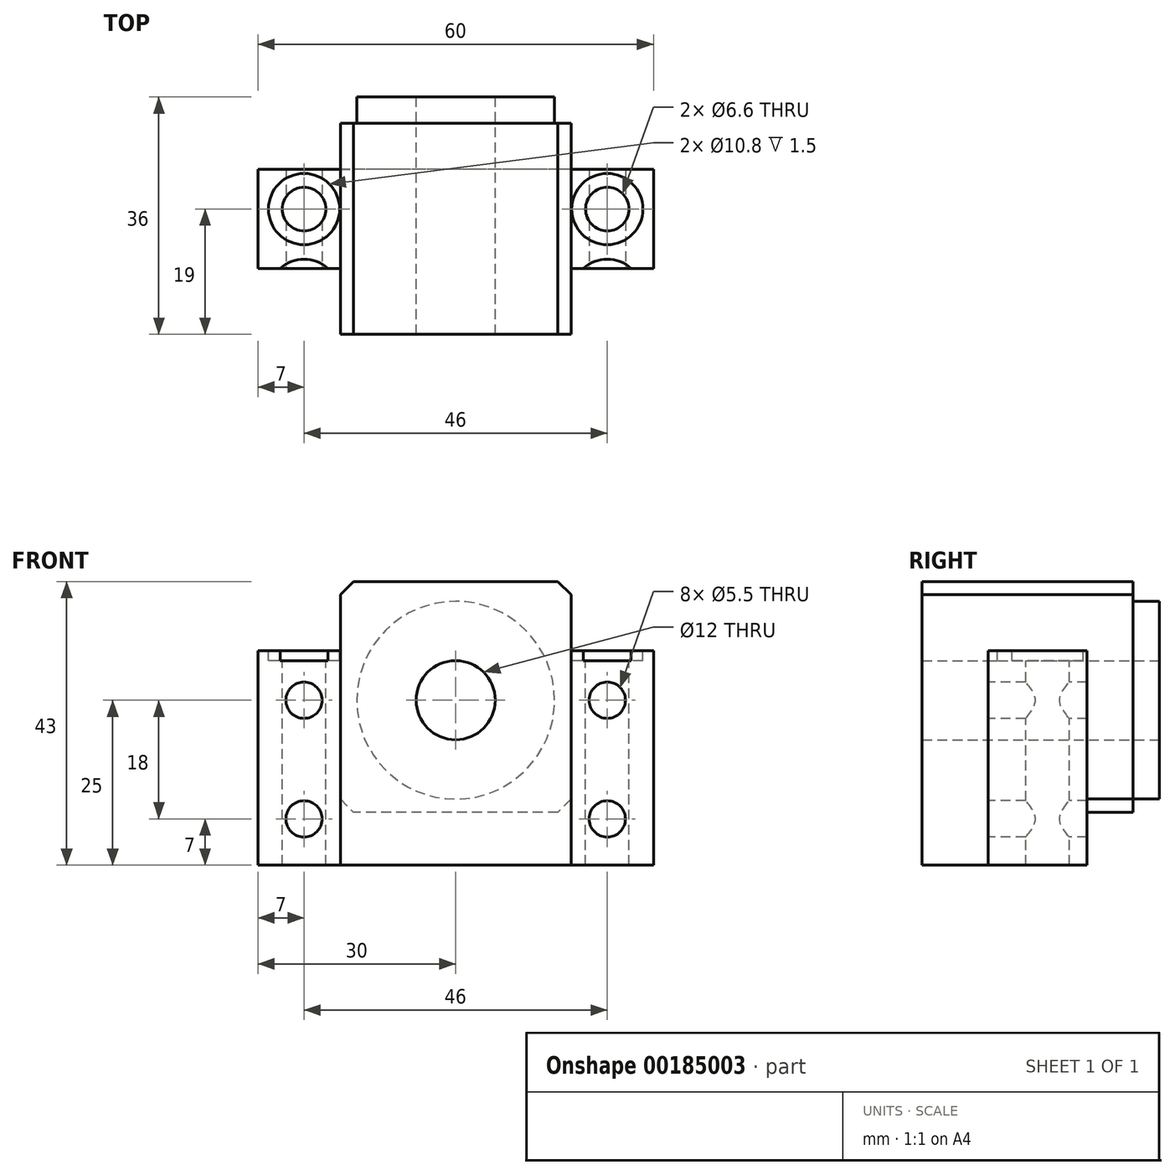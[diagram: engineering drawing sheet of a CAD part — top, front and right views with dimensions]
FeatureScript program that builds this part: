
annotation { "Feature Type Name" : "Feature", "Feature Type Description" : "" }
export const myFeature = defineFeature(function(context is Context, id is Id, definition is map)
    precondition{}
    {
        {
            var Q0;
            Q0=qCreatedBy(makeId("Front.planeOp"),FACE);
            var sketch = newSketch(context, id + "F10", { "sketchPlane" : qUnion([Q0])});
            skLineSegment(sketch, "E0.bottom", {"start": v(30, 16.25) * mm, "end": v(-30, 16.25) * mm});
            skLineSegment(sketch, "E0.top", {"start": v(30, -16.25) * mm, "end": v(-30, -16.25) * mm});
            skLineSegment(sketch, "E0.left", {"start": v(30, 16.25) * mm, "end": v(30, -16.25) * mm});
            skLineSegment(sketch, "E0.right", {"start": v(-30, 16.25) * mm, "end": v(-30, -16.25) * mm});
            skPoint(sketch, "E0.middle", {"position": v(0, 0) * mm});
            skSolve(sketch);
        }
        {
            var Q0;
            Q0=makeQuery(id+"F10.imprint","IMPRINT",FACE,{"disambiguationData":[TD([[makeQuery(id+"F10.imprint","IMPRINT",EDGE,{"derivedFrom":sQuery(id+"F10.wireOp",EDGE,"E0.bottom")}),1.0]])]});
            extrude(context, id + "F11", {"entities" : qUnion([Q0]), "oppositeDirection" : true, "depth" : 25 * mm});
        }
        {
            var Q0;
            Q0=qCreatedBy(makeId("Front.planeOp"),FACE);
            var sketch = newSketch(context, id + "F0", { "sketchPlane" : qUnion([Q0])});
            skLineSegment(sketch, "E1.bottom", {"start": v(17.5, 26.75) * mm, "end": v(-17.5, 26.75) * mm});
            skLineSegment(sketch, "E1.top", {"start": v(17.5, -8.25) * mm, "end": v(-17.5, -8.25) * mm});
            skLineSegment(sketch, "E1.left", {"start": v(17.5, 26.75) * mm, "end": v(17.5, -8.25) * mm});
            skLineSegment(sketch, "E1.right", {"start": v(-17.5, 26.75) * mm, "end": v(-17.5, -8.25) * mm});
            skPoint(sketch, "E1.middle", {"position": v(0, 9.25) * mm});
            skSolve(sketch);
        }
        {
            var Q0;
            Q0=makeQuery(id+"F0.imprint","IMPRINT",FACE,{"disambiguationData":[TD([[makeQuery(id+"F0.imprint","IMPRINT",EDGE,{"derivedFrom":sQuery(id+"F0.wireOp",EDGE,"E1.bottom")}),1.0]])]});
            extrude(context, id + "F12", {"entities" : qUnion([Q0]), "operationType" : NewBodyOperationType.ADD, "oppositeDirection" : true, "depth" : 32 * mm});
        }
        {
            var Q0;
            Q0=makeQuery(id+"F12.opExtrude","CAP_FACE",FACE,{"disambiguationData":[OSD([sQuery(id+"F0.wireOp",EDGE,"E1.bottom"),sQuery(id+"F0.wireOp",EDGE,"E1.top"),sQuery(id+"F0.wireOp",EDGE,"E1.left"),sQuery(id+"F0.wireOp",EDGE,"E1.right")])],"isStart":false});
            var sketch = newSketch(context, id + "F1", { "sketchPlane" : qUnion([Q0])});
            skCircle(sketch, "E2", {"center": v(0, 8.75) * mm, "radius": 6 * mm});
            skSolve(sketch);
        }
        {
            var Q0;
            Q0=makeQuery(id+"F1.imprint","IMPRINT",FACE,{"disambiguationData":[TD([[makeQuery(id+"F1.imprint","IMPRINT",EDGE,{"derivedFrom":sQuery(id+"F1.wireOp",EDGE,"E2")}),1.0]])]});
            var Q1;
            Q1=sQuery(id+"F1.wireOp",EDGE,"E2");
            extrude(context, id + "F13", {"entities" : qUnion([Q0]), "operationType" : NewBodyOperationType.REMOVE, "surfaceEntities" : qUnion([Q1]), "endBound" : BoundingType.THROUGH_ALL, "oppositeDirection" : true, "depth" : 25 * mm});
        }
        {
            var Q0;
            Q0=makeQuery(id+"F12.opExtrude","SWEPT_EDGE",EDGE,{"disambiguationData":[OSD([sQuery(id+"F0.wireOp",EDGE,"E1.bottom"),sQuery(id+"F0.wireOp",EDGE,"E1.right")])]});
            var Q1;
            Q1=makeQuery(id+"F12.opExtrude","SWEPT_EDGE",EDGE,{"disambiguationData":[OSD([sQuery(id+"F0.wireOp",EDGE,"E1.bottom"),sQuery(id+"F0.wireOp",EDGE,"E1.left")])]});
            chamfer(context, id + "F2", {"entities" : qUnion([Q0, Q1]), "width" : 2 * mm, "tangentPropagation" : true});
        }
        {
            var Q0;
            Q0=qCreatedBy(makeId("Front.planeOp"),FACE);
            var sketch = newSketch(context, id + "F3", { "sketchPlane" : qUnion([Q0])});
            skPoint(sketch, "E3.middle", {"position": v(0, -0.25) * mm});
            skCircle(sketch, "E4", {"center": v(23, 8.75) * mm, "radius": 2.75 * mm});
            skCircle(sketch, "E5", {"center": v(23, -9.25) * mm, "radius": 2.75 * mm});
            skCircle(sketch, "E6", {"center": v(-23, -9.25) * mm, "radius": 2.75 * mm});
            skCircle(sketch, "E7", {"center": v(-23, 8.75) * mm, "radius": 2.75 * mm});
            skSolve(sketch);
        }
        {
            var Q0;
            Q0=makeQuery(id+"F3.imprint","IMPRINT",FACE,{"disambiguationData":[TD([[makeQuery(id+"F3.imprint","IMPRINT",EDGE,{"derivedFrom":sQuery(id+"F3.wireOp",EDGE,"E5")}),1.0]])]});
            var Q1;
            Q1=makeQuery(id+"F3.imprint","IMPRINT",FACE,{"disambiguationData":[TD([[makeQuery(id+"F3.imprint","IMPRINT",EDGE,{"derivedFrom":sQuery(id+"F3.wireOp",EDGE,"E4")}),1.0]])]});
            var Q2;
            Q2=makeQuery(id+"F3.imprint","IMPRINT",FACE,{"disambiguationData":[TD([[makeQuery(id+"F3.imprint","IMPRINT",EDGE,{"derivedFrom":sQuery(id+"F3.wireOp",EDGE,"E7")}),1.0]])]});
            var Q3;
            Q3=makeQuery(id+"F3.imprint","IMPRINT",FACE,{"disambiguationData":[TD([[makeQuery(id+"F3.imprint","IMPRINT",EDGE,{"derivedFrom":sQuery(id+"F3.wireOp",EDGE,"E6")}),1.0]])]});
            extrude(context, id + "F14", {"entities" : qUnion([Q0, Q1, Q2, Q3]), "operationType" : NewBodyOperationType.REMOVE, "endBound" : BoundingType.THROUGH_ALL, "oppositeDirection" : true, "depth" : 25 * mm});
        }
        {
            var Q0;
            Q0=makeQuery(id+"F12.opExtrude","SWEPT_EDGE",EDGE,{"disambiguationData":[OSD([sQuery(id+"F0.wireOp",EDGE,"E1.top"),sQuery(id+"F0.wireOp",EDGE,"E1.right")])]});
            var Q1;
            Q1=makeQuery(id+"F12.opExtrude","SWEPT_EDGE",EDGE,{"disambiguationData":[OSD([sQuery(id+"F0.wireOp",EDGE,"E1.top"),sQuery(id+"F0.wireOp",EDGE,"E1.left")])]});
            chamfer(context, id + "F4", {"entities" : qUnion([Q0, Q1]), "width" : 2 * mm, "tangentPropagation" : true});
        }
        {
            var Q0;
            {var subQ0=sQuery(id+"F10.wireOp",EDGE,"E0.right");var subQ3=sQuery(id+"F10.wireOp",EDGE,"E0.bottom");Q0=makeQuery(id+"F12.boolean.opBoolean","SPLIT",FACE,{"disambiguationData":[TD([makeQuery(id+"F11.opExtrude","SWEPT_FACE",FACE,{"disambiguationData":[OSD([subQ0])]})])],"derivedFrom":makeQuery(id+"F11.opExtrude","SWEPT_FACE",FACE,{"disambiguationData":[OSD([subQ3])]})});}
            var sketch = newSketch(context, id + "F5", { "sketchPlane" : qUnion([Q0])});
            skCircle(sketch, "E8", {"center": v(-23, 19) * mm, "radius": 3.3 * mm});
            skCircle(sketch, "E9", {"center": v(-23, 6) * mm, "radius": 3.3 * mm});
            skCircle(sketch, "E10.MirrorC", {"center": v(23, 19) * mm, "radius": 3.3 * mm});
            skCircle(sketch, "E11.MirrorC", {"center": v(23, 6) * mm, "radius": 3.3 * mm});
            skPoint(sketch, "E12.start.orphan", {"position": v(0, 35.82) * mm});
            skSolve(sketch);
        }
        {
            var Q0;
            Q0=sQuery(id+"F5.wireOp",VERTEX,"E9.center");
            var Q1;
            Q1=sQuery(id+"F5.wireOp",VERTEX,"E8.center");
            var Q2;
            Q2=sQuery(id+"F5.wireOp",VERTEX,"E11.MirrorC.center");
            var Q3;
            Q3=sQuery(id+"F5.wireOp",VERTEX,"E10.MirrorC.center");
            var Q4;
            Q4=makeQuery(id+"F11.opExtrude","SWEPT_BODY",BODY,{"disambiguationData":[OSD([sQuery(id+"F10.wireOp",EDGE,"E0.bottom"),sQuery(id+"F10.wireOp",EDGE,"E0.top"),sQuery(id+"F10.wireOp",EDGE,"E0.left"),sQuery(id+"F10.wireOp",EDGE,"E0.right")])]});
            hole(context, id + "F6", {"style" : HoleStyle.C_BORE, "endStyle" : HoleEndStyle.THROUGH, "holeDiameter" : 6.6 * mm, "cBoreDiameter" : 10.8 * mm, "cBoreDepth" : 1.5 * mm, "locations" : qUnion([Q0, Q1, Q2, Q3]), "scope" : qUnion([Q4]), "isTappedThrough" : true});
        }
        {
            var Q0;
            Q0=makeQuery(id+"F12.opExtrude","CAP_FACE",FACE,{"disambiguationData":[OSD([sQuery(id+"F0.wireOp",EDGE,"E1.bottom"),sQuery(id+"F0.wireOp",EDGE,"E1.top"),sQuery(id+"F0.wireOp",EDGE,"E1.left"),sQuery(id+"F0.wireOp",EDGE,"E1.right")])],"isStart":false});
            var sketch = newSketch(context, id + "F15", { "sketchPlane" : qUnion([Q0])});
            skPoint(sketch, "E13.middle", {"position": v(0, 8.75) * mm});
            skPoint(sketch, "E13.right.end.orphan", {"position": v(-18.85, -10.1) * mm});
            skPoint(sketch, "E13.right.start.orphan", {"position": v(-18.85, 27.6) * mm});
            skPoint(sketch, "E13.left.end.orphan", {"position": v(18.85, -10.1) * mm});
            skPoint(sketch, "E13.left.start.orphan", {"position": v(18.85, 27.6) * mm});
            skCircle(sketch, "E14", {"center": v(0, 8.75) * mm, "radius": 15 * mm});
            skSolve(sketch);
        }
        {
            var Q0;
            Q0=makeQuery(id+"F15.imprint","IMPRINT",FACE,{"disambiguationData":[TD([[makeQuery(id+"F15.imprint","IMPRINT",EDGE,{"derivedFrom":sQuery(id+"F15.wireOp",EDGE,"E14")}),1.0]])]});
            var Q1;
            Q1=sQuery(id+"F15.wireOp",EDGE,"E14");
            extrude(context, id + "F7", {"entities" : qUnion([Q0]), "operationType" : NewBodyOperationType.ADD, "surfaceEntities" : qUnion([Q1]), "depth" : 4 * mm});
        }
        {
            var Q0;
            Q0=makeQuery(id+"F12.boolean.opBoolean","MERGE",FACE,{"derivedFrom":[makeQuery(id+"F11.opExtrude","CAP_FACE",FACE,{"disambiguationData":[OSD([sQuery(id+"F10.wireOp",EDGE,"E0.bottom"),sQuery(id+"F10.wireOp",EDGE,"E0.top"),sQuery(id+"F10.wireOp",EDGE,"E0.left"),sQuery(id+"F10.wireOp",EDGE,"E0.right")])],"isStart":true}),makeQuery(id+"F12.opExtrude","CAP_FACE",FACE,{"disambiguationData":[OSD([sQuery(id+"F0.wireOp",EDGE,"E1.bottom"),sQuery(id+"F0.wireOp",EDGE,"E1.top"),sQuery(id+"F0.wireOp",EDGE,"E1.left"),sQuery(id+"F0.wireOp",EDGE,"E1.right")])],"isStart":true})]});
            var sketch = newSketch(context, id + "F8", { "sketchPlane" : qUnion([Q0])});
            skLineSegment(sketch, "E15.bottom", {"start": v(-30, 16.25) * mm, "end": v(-17.5, 16.25) * mm});
            skLineSegment(sketch, "E15.top", {"start": v(-30, -16.25) * mm, "end": v(-17.5, -16.25) * mm});
            skLineSegment(sketch, "E15.left", {"start": v(-30, 16.25) * mm, "end": v(-30, -16.25) * mm});
            skLineSegment(sketch, "E15.right", {"start": v(-17.5, 16.25) * mm, "end": v(-17.5, -16.25) * mm});
            skLineSegment(sketch, "E16.bottom", {"start": v(30, 16.25) * mm, "end": v(17.5, 16.25) * mm});
            skLineSegment(sketch, "E16.top", {"start": v(30, -16.25) * mm, "end": v(17.5, -16.25) * mm});
            skLineSegment(sketch, "E16.left", {"start": v(30, 16.25) * mm, "end": v(30, -16.25) * mm});
            skLineSegment(sketch, "E16.right", {"start": v(17.5, 16.25) * mm, "end": v(17.5, -16.25) * mm});
            skSolve(sketch);
        }
        {
            var Q0;
            Q0 = qSketchRegion(id + "F8", true);
            extrude(context, id + "F9", {"entities" : qUnion([Q0]), "operationType" : NewBodyOperationType.REMOVE, "oppositeDirection" : true, "depth" : 10 * mm});
        }
    });
